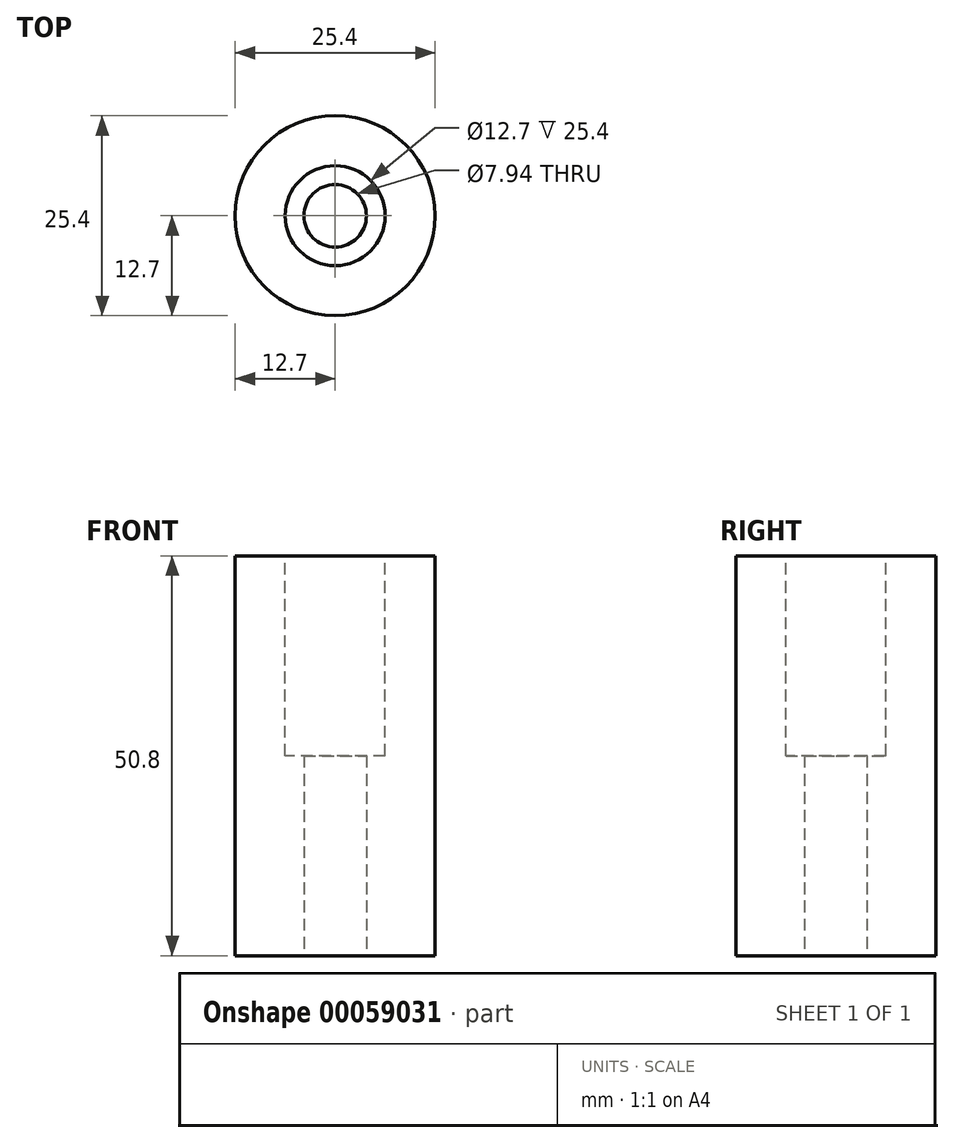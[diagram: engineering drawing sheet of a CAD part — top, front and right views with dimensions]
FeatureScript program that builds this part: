
annotation { "Feature Type Name" : "Feature", "Feature Type Description" : "" }
export const myFeature = defineFeature(function(context is Context, id is Id, definition is map)
    precondition{}
    {
        {
            var Q0;
            Q0=qCreatedBy(makeId("Top.planeOp"),FACE);
            var sketch = newSketch(context, id + "F0", { "sketchPlane" : qUnion([Q0])});
            skCircle(sketch, "E0", {"center": v(0, 0) * mm, "radius": 12.7 * mm});
            skSolve(sketch);
        }
        {
            var Q0;
            Q0=qSketchRegion(id+"F0",true);
            extrude(context, id + "F1", {"entities" : qUnion([Q0]), "depth" : 50.8 * mm});
        }
        {
            var Q0;
            Q0=qSketchRegion(id+"F0",true);
            extrude(context, id + "F2", {"entities" : qUnion([Q0]), "operationType" : NewBodyOperationType.ADD, "depth" : 50.8 * mm});
        }
        {
            var Q0;
            Q0=makeQuery(id+"F1.opExtrude","CAP_FACE",FACE,{"disambiguationData":[OSD([sQuery(id+"F0.wireOp",EDGE,"E0")])],"isStart":false});
            var sketch = newSketch(context, id + "F3", { "sketchPlane" : qUnion([Q0])});
            skCircle(sketch, "E1", {"center": v(0, 0) * mm, "radius": 6.35 * mm});
            skSolve(sketch);
        }
        {
            var Q0;
            Q0=qSketchRegion(id+"F3",true);
            extrude(context, id + "F4", {"entities" : qUnion([Q0]), "operationType" : NewBodyOperationType.REMOVE, "oppositeDirection" : true, "depth" : 25.4 * mm});
        }
        {
            var Q0;
            Q0=makeQuery(id+"F1.opExtrude","CAP_FACE",FACE,{"disambiguationData":[OSD([sQuery(id+"F0.wireOp",EDGE,"E0")])],"isStart":true});
            var sketch = newSketch(context, id + "F5", { "sketchPlane" : qUnion([Q0])});
            skCircle(sketch, "E2", {"center": v(0, 0) * mm, "radius": 3.97 * mm});
            skSolve(sketch);
        }
        {
            var Q0;
            Q0=qSketchRegion(id+"F5",true);
            extrude(context, id + "F6", {"entities" : qUnion([Q0]), "operationType" : NewBodyOperationType.REMOVE, "oppositeDirection" : true, "depth" : 25.4 * mm});
        }
    });
